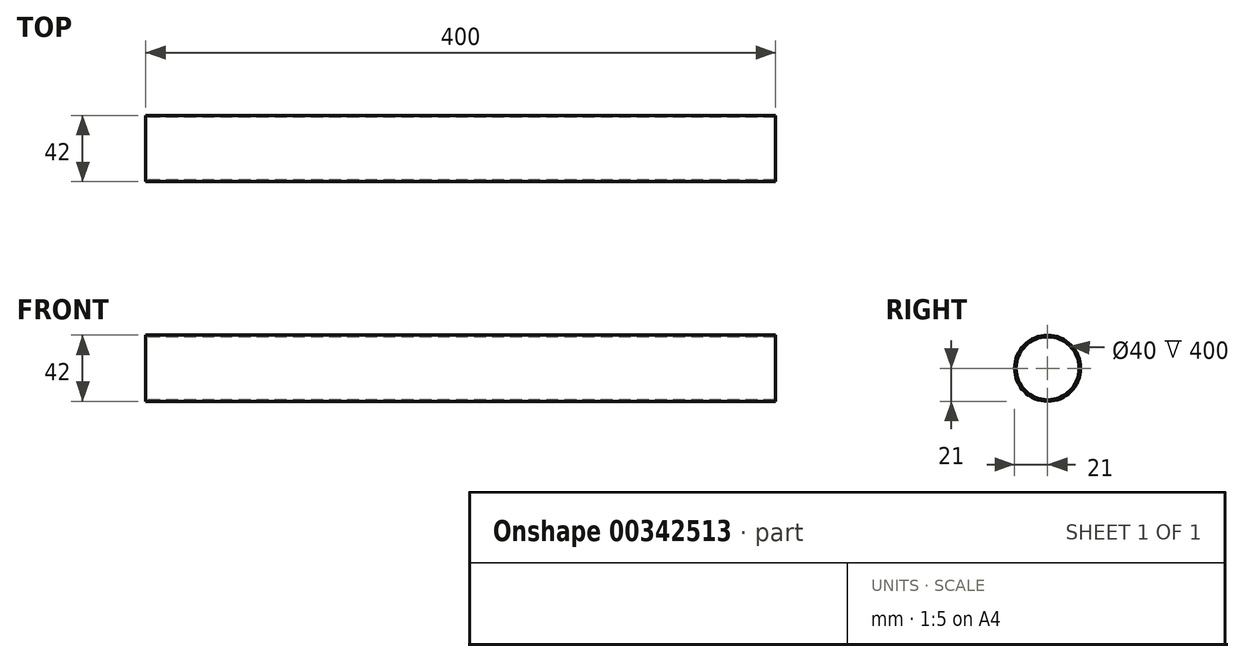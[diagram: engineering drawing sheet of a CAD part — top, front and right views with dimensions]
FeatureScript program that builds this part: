
annotation { "Feature Type Name" : "Feature", "Feature Type Description" : "" }
export const myFeature = defineFeature(function(context is Context, id is Id, definition is map)
    precondition{}
    {
        {
            var Q0;
            Q0=qCreatedBy(makeId("Right.planeOp"),FACE);
            var sketch = newSketch(context, id + "F0", { "sketchPlane" : qUnion([Q0])});
            skCircle(sketch, "E0", {"center": v(0, 0) * mm, "radius": 21 * mm});
            skCircle(sketch, "E1", {"center": v(0, 0) * mm, "radius": 20 * mm});
            skSolve(sketch);
        }
        {
            var Q0;
            Q0=makeQuery(id+"F0.imprint","IMPRINT",FACE,{"disambiguationData":[TD([[makeQuery(id+"F0.imprint","IMPRINT",EDGE,{"derivedFrom":sQuery(id+"F0.wireOp",EDGE,"E0")}),1.0]])]});
            extrude(context, id + "F1", {"entities" : qUnion([Q0]), "depth" : 400 * mm});
        }
    });
